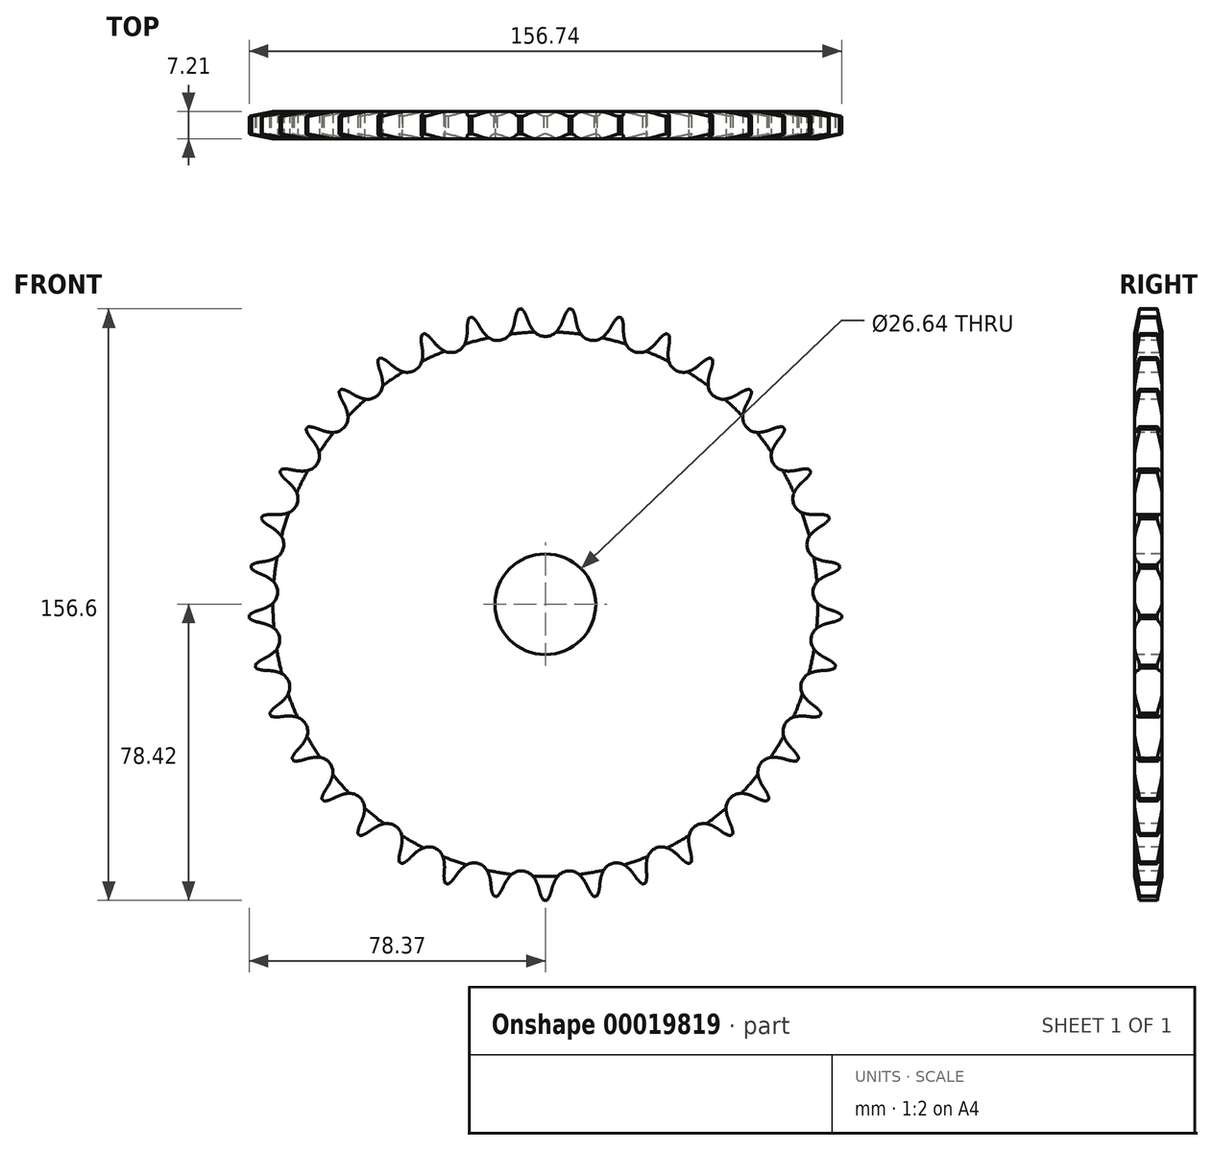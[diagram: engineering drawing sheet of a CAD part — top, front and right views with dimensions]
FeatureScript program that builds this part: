
annotation { "Feature Type Name" : "Feature", "Feature Type Description" : "" }
export const myFeature = defineFeature(function(context is Context, id is Id, definition is map)
    precondition{}
    {
        {
            var Q0;
            Q0=qCreatedBy(makeId("Right.planeOp"),FACE);
            var sketch = newSketch(context, id + "F0", { "sketchPlane" : qUnion([Q0])});
            skLineSegment(sketch, "E0.bottom", {"start": v(0, 78.42) * mm, "end": v(7.21, 78.42) * mm});
            skLineSegment(sketch, "E0.top", {"start": v(0, 13.32) * mm, "end": v(7.21, 13.32) * mm});
            skLineSegment(sketch, "E0.left", {"start": v(0, 78.42) * mm, "end": v(0, 13.32) * mm});
            skLineSegment(sketch, "E0.right", {"start": v(7.21, 78.42) * mm, "end": v(7.21, 13.32) * mm});
            skLineSegment(sketch, "E1", {"start": v(0, 0) * mm, "end": v(19.43, 0) * mm, "construction": true});
            skLineSegment(sketch, "E2.MirrorCS", {"start": v(0, -78.42) * mm, "end": v(7.21, -78.42) * mm});
            skLineSegment(sketch, "E3.MirrorCS", {"start": v(0, -78.42) * mm, "end": v(0, -13.32) * mm});
            skLineSegment(sketch, "E4.MirrorCS", {"start": v(7.21, -78.42) * mm, "end": v(7.21, -13.32) * mm});
            skLineSegment(sketch, "E5.MirrorCS", {"start": v(0, -13.32) * mm, "end": v(7.21, -13.32) * mm});
            skSolve(sketch);
        }
        {
            var Q0;
            Q0=makeQuery(id+"F0.imprint","IMPRINT",FACE,{"disambiguationData":[TD([[makeQuery(id+"F0.imprint","IMPRINT",EDGE,{"derivedFrom":sQuery(id+"F0.wireOp",EDGE,"E0.bottom")}),-1.0]])]});
            var Q1;
            Q1=sQuery(id+"F0.wireOp",EDGE,"E1");
            revolve(context, id + "F1", {"entities" : qUnion([Q0]), "axis" : qUnion([Q1]), "revolveType" : RevolveType.FULL});
        }
        {
            var Q0;
            Q0=makeQuery(id+"F1.opRevolve","SWEPT_EDGE",EDGE,{"disambiguationData":[OSD([sQuery(id+"F0.wireOp",EDGE,"E0.bottom"),sQuery(id+"F0.wireOp",EDGE,"E0.left")])]});
            var Q1;
            Q1=makeQuery(id+"F1.opRevolve","SWEPT_EDGE",EDGE,{"disambiguationData":[OSD([sQuery(id+"F0.wireOp",EDGE,"E0.bottom"),sQuery(id+"F0.wireOp",EDGE,"E0.right")])]});
            chamfer(context, id + "F2", {"entities" : qUnion([Q0, Q1]), "chamferType" : ChamferType.TWO_OFFSETS, "width1" : 1.27 * mm, "oppositeDirection" : true, "width2" : 6.35 * mm, "tangentPropagation" : true});
        }
        {
            var Q0;
            Q0=makeQuery(id+"F1.opRevolve","SWEPT_FACE",FACE,{"disambiguationData":[OSD([sQuery(id+"F0.wireOp",EDGE,"E0.left")])]});
            var sketch = newSketch(context, id + "F3", { "sketchPlane" : qUnion([Q0])});
            skCircle(sketch, "E6", {"center": v(0, 0) * mm, "radius": 74.88 * mm, "construction": true});
            skLineSegment(sketch, "E7", {"start": v(0, 0) * mm, "end": v(0, 74.88) * mm, "construction": true});
            skLineSegment(sketch, "E8", {"start": v(0, 74.88) * mm, "end": v(50.33, 74.88) * mm, "construction": true});
            skLineSegment(sketch, "E9", {"start": v(0, 74.88) * mm, "end": v(5.11, 78.68) * mm, "construction": true});
            skLineSegment(sketch, "E10", {"start": v(5.11, 78.68) * mm, "end": v(-4.63, 75.1) * mm, "construction": true});
            skLineSegment(sketch, "E11", {"start": v(-4.63, 75.1) * mm, "end": v(-4.63, 75.1) * mm});
            skLineSegment(sketch, "E12", {"start": v(0, 0) * mm, "end": v(-6.7, 78.67) * mm, "construction": true});
            skArc(sketch, "E13", {"start": v(-6.7, 78.67) * mm, "mid": v(-16.4, 70.36) * mm, "end": v(-5.01, 76.15) * mm, "construction": true});
            skArc(sketch, "E14", {"start": v(-5.01, 76.15) * mm, "mid": v(-5.7, 77.5) * mm, "end": v(-6.7, 78.67) * mm});
            skLineSegment(sketch, "E15", {"start": v(-5.01, 76.15) * mm, "end": v(-8.52, 85.73) * mm, "construction": true});
            skLineSegment(sketch, "E16", {"start": v(-4.63, 75.1) * mm, "end": v(-5.01, 76.15) * mm});
            skArc(sketch, "E17", {"start": v(-4.63, 75.1) * mm, "mid": v(-4.02, 73.75) * mm, "end": v(-3.22, 72.49) * mm});
            skArc(sketch, "E18", {"start": v(-3.22, 72.49) * mm, "mid": v(14.24, 83.6) * mm, "end": v(-4.63, 75.1) * mm, "construction": true});
            skArc(sketch, "E19", {"start": v(0, 70.87) * mm, "mid": v(1.8, 78.46) * mm, "end": v(-3.22, 72.49) * mm, "construction": true});
            skArc(sketch, "E20", {"start": v(-3.22, 72.49) * mm, "mid": v(-1.8, 71.3) * mm, "end": v(0, 70.87) * mm});
            skArc(sketch, "E21.MirrorCS", {"start": v(3.22, 72.49) * mm, "mid": v(1.8, 71.3) * mm, "end": v(0, 70.87) * mm});
            skArc(sketch, "E22.MirrorCS", {"start": v(4.63, 75.1) * mm, "mid": v(4.02, 73.75) * mm, "end": v(3.22, 72.49) * mm});
            skLineSegment(sketch, "E23.MirrorCS", {"start": v(4.63, 75.1) * mm, "end": v(5.01, 76.15) * mm});
            skArc(sketch, "E24.MirrorCS", {"start": v(5.01, 76.15) * mm, "mid": v(5.7, 77.5) * mm, "end": v(6.7, 78.67) * mm});
            skArc(sketch, "E25.1.0", {"start": v(-17.81, 74.2) * mm, "mid": v(-18.72, 75.43) * mm, "end": v(-19.9, 76.4) * mm});
            skLineSegment(sketch, "E25.1.1", {"start": v(-17.26, 73.24) * mm, "end": v(-17.81, 74.2) * mm});
            skArc(sketch, "E25.1.2", {"start": v(-17.26, 73.24) * mm, "mid": v(-16.42, 72) * mm, "end": v(-15.42, 70.9) * mm});
            skArc(sketch, "E25.1.3", {"start": v(-15.42, 70.9) * mm, "mid": v(-13.82, 69.97) * mm, "end": v(-11.98, 69.85) * mm});
            skArc(sketch, "E25.1.4", {"start": v(-9.08, 71.99) * mm, "mid": v(-10.27, 70.58) * mm, "end": v(-11.98, 69.85) * mm});
            skArc(sketch, "E25.1.5", {"start": v(-8.13, 74.81) * mm, "mid": v(-8.5, 73.37) * mm, "end": v(-9.08, 71.99) * mm});
            skLineSegment(sketch, "E25.1.6", {"start": v(-8.13, 74.81) * mm, "end": v(-7.93, 75.9) * mm});
            skArc(sketch, "E25.1.7", {"start": v(-7.93, 75.9) * mm, "mid": v(-7.48, 77.36) * mm, "end": v(-6.7, 78.67) * mm});
            skArc(sketch, "E25.2.0", {"start": v(-30.1, 70.13) * mm, "mid": v(-31.2, 71.18) * mm, "end": v(-32.52, 71.94) * mm});
            skLineSegment(sketch, "E25.2.1", {"start": v(-29.39, 69.27) * mm, "end": v(-30.1, 70.13) * mm});
            skArc(sketch, "E25.2.2", {"start": v(-29.39, 69.27) * mm, "mid": v(-28.36, 68.2) * mm, "end": v(-27.18, 67.28) * mm});
            skArc(sketch, "E25.2.3", {"start": v(-27.18, 67.28) * mm, "mid": v(-25.45, 66.62) * mm, "end": v(-23.6, 66.82) * mm});
            skArc(sketch, "E25.2.4", {"start": v(-21.11, 69.42) * mm, "mid": v(-22.05, 67.82) * mm, "end": v(-23.6, 66.82) * mm});
            skArc(sketch, "E25.2.5", {"start": v(-20.65, 72.36) * mm, "mid": v(-20.78, 70.87) * mm, "end": v(-21.11, 69.42) * mm});
            skLineSegment(sketch, "E25.2.6", {"start": v(-20.65, 72.36) * mm, "end": v(-20.64, 73.47) * mm});
            skArc(sketch, "E25.2.7", {"start": v(-20.64, 73.47) * mm, "mid": v(-20.44, 74.98) * mm, "end": v(-19.9, 76.4) * mm});
            skArc(sketch, "E25.3.0", {"start": v(-41.52, 64.03) * mm, "mid": v(-42.78, 64.88) * mm, "end": v(-44.21, 65.41) * mm});
            skLineSegment(sketch, "E25.3.1", {"start": v(-40.67, 63.31) * mm, "end": v(-41.52, 64.03) * mm});
            skArc(sketch, "E25.3.2", {"start": v(-40.67, 63.31) * mm, "mid": v(-39.48, 62.42) * mm, "end": v(-38.16, 61.71) * mm});
            skArc(sketch, "E25.3.3", {"start": v(-38.16, 61.71) * mm, "mid": v(-36.34, 61.37) * mm, "end": v(-34.56, 61.87) * mm});
            skArc(sketch, "E25.3.4", {"start": v(-32.54, 64.85) * mm, "mid": v(-33.2, 63.12) * mm, "end": v(-34.56, 61.87) * mm});
            skArc(sketch, "E25.3.5", {"start": v(-32.59, 67.83) * mm, "mid": v(-32.46, 66.34) * mm, "end": v(-32.54, 64.85) * mm});
            skLineSegment(sketch, "E25.3.6", {"start": v(-32.59, 67.83) * mm, "end": v(-32.76, 68.92) * mm});
            skArc(sketch, "E25.3.7", {"start": v(-32.76, 68.92) * mm, "mid": v(-32.82, 70.45) * mm, "end": v(-32.52, 71.94) * mm});
            skArc(sketch, "E25.4.0", {"start": v(-51.74, 56.1) * mm, "mid": v(-53.13, 56.72) * mm, "end": v(-54.63, 57) * mm});
            skLineSegment(sketch, "E25.4.1", {"start": v(-50.79, 55.53) * mm, "end": v(-51.74, 56.1) * mm});
            skArc(sketch, "E25.4.2", {"start": v(-50.79, 55.53) * mm, "mid": v(-49.46, 54.85) * mm, "end": v(-48.04, 54.38) * mm});
            skArc(sketch, "E25.4.3", {"start": v(-48.04, 54.38) * mm, "mid": v(-46.2, 54.34) * mm, "end": v(-44.52, 55.14) * mm});
            skArc(sketch, "E25.4.4", {"start": v(-43.03, 58.42) * mm, "mid": v(-43.39, 56.6) * mm, "end": v(-44.52, 55.14) * mm});
            skArc(sketch, "E25.4.5", {"start": v(-43.58, 61.35) * mm, "mid": v(-43.2, 59.9) * mm, "end": v(-43.03, 58.42) * mm});
            skLineSegment(sketch, "E25.4.6", {"start": v(-43.58, 61.35) * mm, "end": v(-43.94, 62.4) * mm});
            skArc(sketch, "E25.4.7", {"start": v(-43.94, 62.4) * mm, "mid": v(-44.25, 63.89) * mm, "end": v(-44.21, 65.41) * mm});
            skArc(sketch, "E25.5.0", {"start": v(-60.48, 46.55) * mm, "mid": v(-61.95, 46.93) * mm, "end": v(-63.48, 46.95) * mm});
            skLineSegment(sketch, "E25.5.1", {"start": v(-59.44, 46.14) * mm, "end": v(-60.48, 46.55) * mm});
            skArc(sketch, "E25.5.2", {"start": v(-59.44, 46.14) * mm, "mid": v(-58.02, 45.7) * mm, "end": v(-56.54, 45.48) * mm});
            skArc(sketch, "E25.5.3", {"start": v(-56.54, 45.48) * mm, "mid": v(-54.71, 45.75) * mm, "end": v(-53.2, 46.82) * mm});
            skArc(sketch, "E25.5.4", {"start": v(-52.29, 50.3) * mm, "mid": v(-52.33, 48.46) * mm, "end": v(-53.2, 46.82) * mm});
            skArc(sketch, "E25.5.5", {"start": v(-53.32, 53.1) * mm, "mid": v(-52.7, 51.74) * mm, "end": v(-52.29, 50.3) * mm});
            skLineSegment(sketch, "E25.5.6", {"start": v(-53.32, 53.1) * mm, "end": v(-53.85, 54.07) * mm});
            skArc(sketch, "E25.5.7", {"start": v(-53.85, 54.07) * mm, "mid": v(-54.42, 55.5) * mm, "end": v(-54.63, 57) * mm});
            skArc(sketch, "E25.6.0", {"start": v(-67.47, 35.66) * mm, "mid": v(-69, 35.78) * mm, "end": v(-70.5, 35.54) * mm});
            skLineSegment(sketch, "E25.6.1", {"start": v(-66.39, 35.43) * mm, "end": v(-67.47, 35.66) * mm});
            skArc(sketch, "E25.6.2", {"start": v(-66.39, 35.43) * mm, "mid": v(-64.9, 35.24) * mm, "end": v(-63.41, 35.27) * mm});
            skArc(sketch, "E25.6.3", {"start": v(-63.41, 35.27) * mm, "mid": v(-61.66, 35.85) * mm, "end": v(-60.35, 37.16) * mm});
            skArc(sketch, "E25.6.4", {"start": v(-60.04, 40.75) * mm, "mid": v(-59.77, 38.92) * mm, "end": v(-60.35, 37.16) * mm});
            skArc(sketch, "E25.6.5", {"start": v(-61.53, 43.32) * mm, "mid": v(-60.7, 42.09) * mm, "end": v(-60.04, 40.75) * mm});
            skLineSegment(sketch, "E25.6.6", {"start": v(-61.53, 43.32) * mm, "end": v(-62.21, 44.2) * mm});
            skArc(sketch, "E25.6.7", {"start": v(-62.21, 44.2) * mm, "mid": v(-63.01, 45.5) * mm, "end": v(-63.48, 46.95) * mm});
            skArc(sketch, "E25.7.0", {"start": v(-72.53, 23.74) * mm, "mid": v(-74.05, 23.6) * mm, "end": v(-75.5, 23.12) * mm});
            skLineSegment(sketch, "E25.7.1", {"start": v(-71.42, 23.7) * mm, "end": v(-72.53, 23.74) * mm});
            skArc(sketch, "E25.7.2", {"start": v(-71.42, 23.7) * mm, "mid": v(-69.93, 23.77) * mm, "end": v(-68.46, 24.04) * mm});
            skArc(sketch, "E25.7.3", {"start": v(-68.46, 24.04) * mm, "mid": v(-66.83, 24.91) * mm, "end": v(-65.76, 26.42) * mm});
            skArc(sketch, "E25.7.4", {"start": v(-66.06, 30.01) * mm, "mid": v(-65.48, 28.25) * mm, "end": v(-65.76, 26.42) * mm});
            skArc(sketch, "E25.7.5", {"start": v(-67.96, 32.3) * mm, "mid": v(-66.93, 31.23) * mm, "end": v(-66.06, 30.01) * mm});
            skLineSegment(sketch, "E25.7.6", {"start": v(-67.96, 32.3) * mm, "end": v(-68.79, 33.05) * mm});
            skArc(sketch, "E25.7.7", {"start": v(-68.79, 33.05) * mm, "mid": v(-69.8, 34.2) * mm, "end": v(-70.5, 35.54) * mm});
            skArc(sketch, "E25.8.0", {"start": v(-75.5, 11.14) * mm, "mid": v(-76.97, 10.75) * mm, "end": v(-78.31, 10.03) * mm});
            skLineSegment(sketch, "E25.8.1", {"start": v(-74.4, 11.3) * mm, "end": v(-75.5, 11.14) * mm});
            skArc(sketch, "E25.8.2", {"start": v(-74.4, 11.3) * mm, "mid": v(-72.94, 11.6) * mm, "end": v(-71.54, 12.13) * mm});
            skArc(sketch, "E25.8.3", {"start": v(-71.54, 12.13) * mm, "mid": v(-70.08, 13.26) * mm, "end": v(-69.28, 14.93) * mm});
            skArc(sketch, "E25.8.4", {"start": v(-70.18, 18.42) * mm, "mid": v(-69.32, 16.78) * mm, "end": v(-69.28, 14.93) * mm});
            skArc(sketch, "E25.8.5", {"start": v(-72.45, 20.35) * mm, "mid": v(-71.24, 19.47) * mm, "end": v(-70.18, 18.42) * mm});
            skLineSegment(sketch, "E25.8.6", {"start": v(-72.45, 20.35) * mm, "end": v(-73.38, 20.94) * mm});
            skArc(sketch, "E25.8.7", {"start": v(-73.38, 20.94) * mm, "mid": v(-74.57, 21.9) * mm, "end": v(-75.5, 23.12) * mm});
            skArc(sketch, "E25.9.0", {"start": v(-76.3, -1.78) * mm, "mid": v(-77.68, -2.4) * mm, "end": v(-78.88, -3.35) * mm});
            skLineSegment(sketch, "E25.9.1", {"start": v(-75.24, -1.44) * mm, "end": v(-76.3, -1.78) * mm});
            skArc(sketch, "E25.9.2", {"start": v(-75.24, -1.44) * mm, "mid": v(-73.85, -0.89) * mm, "end": v(-72.56, -0.14) * mm});
            skArc(sketch, "E25.9.3", {"start": v(-72.56, -0.14) * mm, "mid": v(-71.3, 1.23) * mm, "end": v(-70.8, 3) * mm});
            skArc(sketch, "E25.9.4", {"start": v(-72.29, 6.3) * mm, "mid": v(-71.16, 4.82) * mm, "end": v(-70.8, 3) * mm});
            skArc(sketch, "E25.9.5", {"start": v(-74.84, 7.82) * mm, "mid": v(-73.5, 7.15) * mm, "end": v(-72.29, 6.3) * mm});
            skLineSegment(sketch, "E25.9.6", {"start": v(-74.84, 7.82) * mm, "end": v(-75.87, 8.24) * mm});
            skArc(sketch, "E25.9.7", {"start": v(-75.87, 8.24) * mm, "mid": v(-77.2, 8.99) * mm, "end": v(-78.31, 10.03) * mm});
            skArc(sketch, "E25.10.0", {"start": v(-74.9, -14.65) * mm, "mid": v(-76.16, -15.5) * mm, "end": v(-77.18, -16.63) * mm});
            skLineSegment(sketch, "E25.10.1", {"start": v(-73.91, -14.14) * mm, "end": v(-74.9, -14.65) * mm});
            skArc(sketch, "E25.10.2", {"start": v(-73.91, -14.14) * mm, "mid": v(-72.64, -13.35) * mm, "end": v(-71.5, -12.4) * mm});
            skArc(sketch, "E25.10.3", {"start": v(-71.5, -12.4) * mm, "mid": v(-70.5, -10.84) * mm, "end": v(-70.3, -9) * mm});
            skArc(sketch, "E25.10.4", {"start": v(-72.3, -6.02) * mm, "mid": v(-70.95, -7.27) * mm, "end": v(-70.3, -9) * mm});
            skArc(sketch, "E25.10.5", {"start": v(-75.09, -4.95) * mm, "mid": v(-73.66, -5.38) * mm, "end": v(-72.3, -6.02) * mm});
            skLineSegment(sketch, "E25.10.6", {"start": v(-75.09, -4.95) * mm, "end": v(-76.17, -4.7) * mm});
            skArc(sketch, "E25.10.7", {"start": v(-76.17, -4.7) * mm, "mid": v(-77.6, -4.19) * mm, "end": v(-78.88, -3.35) * mm});
            skArc(sketch, "E25.11.0", {"start": v(-71.34, -27.1) * mm, "mid": v(-72.44, -28.15) * mm, "end": v(-73.26, -29.44) * mm});
            skLineSegment(sketch, "E25.11.1", {"start": v(-70.46, -26.42) * mm, "end": v(-71.34, -27.1) * mm});
            skArc(sketch, "E25.11.2", {"start": v(-70.46, -26.42) * mm, "mid": v(-69.34, -25.44) * mm, "end": v(-68.37, -24.3) * mm});
            skArc(sketch, "E25.11.3", {"start": v(-68.37, -24.3) * mm, "mid": v(-67.64, -22.6) * mm, "end": v(-67.76, -20.75) * mm});
            skArc(sketch, "E25.11.4", {"start": v(-70.25, -18.15) * mm, "mid": v(-68.7, -19.16) * mm, "end": v(-67.76, -20.75) * mm});
            skArc(sketch, "E25.11.5", {"start": v(-73.17, -17.56) * mm, "mid": v(-71.7, -17.75) * mm, "end": v(-70.25, -18.15) * mm});
            skLineSegment(sketch, "E25.11.6", {"start": v(-73.17, -17.56) * mm, "end": v(-74.28, -17.5) * mm});
            skArc(sketch, "E25.11.7", {"start": v(-74.28, -17.5) * mm, "mid": v(-75.78, -17.24) * mm, "end": v(-77.18, -16.63) * mm});
            skArc(sketch, "E25.12.0", {"start": v(-65.74, -38.76) * mm, "mid": v(-66.64, -39.99) * mm, "end": v(-67.23, -41.4) * mm});
            skLineSegment(sketch, "E25.12.1", {"start": v(-64.98, -37.95) * mm, "end": v(-65.74, -38.76) * mm});
            skArc(sketch, "E25.12.2", {"start": v(-64.98, -37.95) * mm, "mid": v(-64.04, -36.8) * mm, "end": v(-63.28, -35.5) * mm});
            skArc(sketch, "E25.12.3", {"start": v(-63.28, -35.5) * mm, "mid": v(-62.85, -33.7) * mm, "end": v(-63.28, -31.9) * mm});
            skArc(sketch, "E25.12.4", {"start": v(-66.17, -29.76) * mm, "mid": v(-64.47, -30.5) * mm, "end": v(-63.28, -31.9) * mm});
            skArc(sketch, "E25.12.5", {"start": v(-69.15, -29.68) * mm, "mid": v(-67.66, -29.61) * mm, "end": v(-66.17, -29.76) * mm});
            skLineSegment(sketch, "E25.12.6", {"start": v(-69.15, -29.68) * mm, "end": v(-70.25, -29.8) * mm});
            skArc(sketch, "E25.12.7", {"start": v(-70.25, -29.8) * mm, "mid": v(-71.78, -29.8) * mm, "end": v(-73.26, -29.44) * mm});
            skArc(sketch, "E25.13.0", {"start": v(-58.24, -49.31) * mm, "mid": v(-58.92, -50.68) * mm, "end": v(-59.27, -52.16) * mm});
            skLineSegment(sketch, "E25.13.1", {"start": v(-57.63, -48.39) * mm, "end": v(-58.24, -49.31) * mm});
            skArc(sketch, "E25.13.2", {"start": v(-57.63, -48.39) * mm, "mid": v(-56.9, -47.08) * mm, "end": v(-56.37, -45.7) * mm});
            skArc(sketch, "E25.13.3", {"start": v(-56.37, -45.7) * mm, "mid": v(-56.25, -43.84) * mm, "end": v(-56.98, -42.14) * mm});
            skArc(sketch, "E25.13.4", {"start": v(-60.2, -40.52) * mm, "mid": v(-58.4, -40.95) * mm, "end": v(-56.98, -42.14) * mm});
            skArc(sketch, "E25.13.5", {"start": v(-63.14, -40.94) * mm, "mid": v(-61.68, -40.62) * mm, "end": v(-60.2, -40.52) * mm});
            skLineSegment(sketch, "E25.13.6", {"start": v(-63.14, -40.94) * mm, "end": v(-64.2, -41.25) * mm});
            skArc(sketch, "E25.13.7", {"start": v(-64.2, -41.25) * mm, "mid": v(-65.7, -41.5) * mm, "end": v(-67.23, -41.4) * mm});
            skArc(sketch, "E25.14.0", {"start": v(-49.07, -58.45) * mm, "mid": v(-49.51, -59.9) * mm, "end": v(-49.6, -61.43) * mm});
            skLineSegment(sketch, "E25.14.1", {"start": v(-48.63, -57.43) * mm, "end": v(-49.07, -58.45) * mm});
            skArc(sketch, "E25.14.2", {"start": v(-48.63, -57.43) * mm, "mid": v(-48.13, -56.02) * mm, "end": v(-47.83, -54.56) * mm});
            skArc(sketch, "E25.14.3", {"start": v(-47.83, -54.56) * mm, "mid": v(-48.03, -52.72) * mm, "end": v(-49.04, -51.17) * mm});
            skArc(sketch, "E25.14.4", {"start": v(-52.48, -50.1) * mm, "mid": v(-50.63, -50.23) * mm, "end": v(-49.04, -51.17) * mm});
            skArc(sketch, "E25.14.5", {"start": v(-55.31, -51.02) * mm, "mid": v(-53.93, -50.46) * mm, "end": v(-52.48, -50.1) * mm});
            skLineSegment(sketch, "E25.14.6", {"start": v(-55.31, -51.02) * mm, "end": v(-56.31, -51.5) * mm});
            skArc(sketch, "E25.14.7", {"start": v(-56.31, -51.5) * mm, "mid": v(-57.75, -52.01) * mm, "end": v(-59.27, -52.16) * mm});
            skArc(sketch, "E25.15.0", {"start": v(-38.49, -65.9) * mm, "mid": v(-38.68, -67.41) * mm, "end": v(-38.5, -68.93) * mm});
            skLineSegment(sketch, "E25.15.1", {"start": v(-38.22, -64.82) * mm, "end": v(-38.49, -65.9) * mm});
            skArc(sketch, "E25.15.2", {"start": v(-38.22, -64.82) * mm, "mid": v(-37.97, -63.35) * mm, "end": v(-37.93, -61.86) * mm});
            skArc(sketch, "E25.15.3", {"start": v(-37.93, -61.86) * mm, "mid": v(-38.43, -60.08) * mm, "end": v(-39.69, -58.72) * mm});
            skArc(sketch, "E25.15.4", {"start": v(-43.26, -58.26) * mm, "mid": v(-41.42, -58.06) * mm, "end": v(-39.69, -58.72) * mm});
            skArc(sketch, "E25.15.5", {"start": v(-45.9, -59.63) * mm, "mid": v(-44.63, -58.85) * mm, "end": v(-43.26, -58.26) * mm});
            skLineSegment(sketch, "E25.15.6", {"start": v(-45.9, -59.63) * mm, "end": v(-46.8, -60.28) * mm});
            skArc(sketch, "E25.15.7", {"start": v(-46.8, -60.28) * mm, "mid": v(-48.13, -61.02) * mm, "end": v(-49.6, -61.43) * mm});
            skArc(sketch, "E25.16.0", {"start": v(-26.8, -71.45) * mm, "mid": v(-26.73, -72.98) * mm, "end": v(-26.3, -74.44) * mm});
            skLineSegment(sketch, "E25.16.1", {"start": v(-26.72, -70.35) * mm, "end": v(-26.8, -71.45) * mm});
            skArc(sketch, "E25.16.2", {"start": v(-26.72, -70.35) * mm, "mid": v(-26.71, -68.86) * mm, "end": v(-26.93, -67.38) * mm});
            skArc(sketch, "E25.16.3", {"start": v(-26.93, -67.38) * mm, "mid": v(-27.73, -65.7) * mm, "end": v(-29.2, -64.58) * mm});
            skArc(sketch, "E25.16.4", {"start": v(-32.79, -64.73) * mm, "mid": v(-31, -64.23) * mm, "end": v(-29.2, -64.58) * mm});
            skArc(sketch, "E25.16.5", {"start": v(-35.16, -66.53) * mm, "mid": v(-34.04, -65.54) * mm, "end": v(-32.79, -64.73) * mm});
            skLineSegment(sketch, "E25.16.6", {"start": v(-35.16, -66.53) * mm, "end": v(-35.94, -67.32) * mm});
            skArc(sketch, "E25.16.7", {"start": v(-35.94, -67.32) * mm, "mid": v(-37.12, -68.28) * mm, "end": v(-38.5, -68.93) * mm});
            skArc(sketch, "E25.17.0", {"start": v(-14.34, -74.96) * mm, "mid": v(-14.01, -76.45) * mm, "end": v(-13.34, -77.82) * mm});
            skLineSegment(sketch, "E25.17.1", {"start": v(-14.44, -73.85) * mm, "end": v(-14.34, -74.96) * mm});
            skArc(sketch, "E25.17.2", {"start": v(-14.44, -73.85) * mm, "mid": v(-14.7, -72.38) * mm, "end": v(-15.15, -70.96) * mm});
            skArc(sketch, "E25.17.3", {"start": v(-15.15, -70.96) * mm, "mid": v(-16.22, -69.45) * mm, "end": v(-17.86, -68.58) * mm});
            skArc(sketch, "E25.17.4", {"start": v(-21.38, -69.34) * mm, "mid": v(-19.7, -68.54) * mm, "end": v(-17.86, -68.58) * mm});
            skArc(sketch, "E25.17.5", {"start": v(-23.4, -71.52) * mm, "mid": v(-22.47, -70.35) * mm, "end": v(-21.38, -69.34) * mm});
            skLineSegment(sketch, "E25.17.6", {"start": v(-23.4, -71.52) * mm, "end": v(-24.04, -72.43) * mm});
            skArc(sketch, "E25.17.7", {"start": v(-24.04, -72.43) * mm, "mid": v(-25.05, -73.57) * mm, "end": v(-26.3, -74.44) * mm});
            skArc(sketch, "E25.18.0", {"start": v(-1.46, -76.3) * mm, "mid": v(-0.89, -77.71) * mm, "end": v(0, -78.95) * mm});
            skLineSegment(sketch, "E25.18.1", {"start": v(-1.75, -75.23) * mm, "end": v(-1.46, -76.3) * mm});
            skArc(sketch, "E25.18.2", {"start": v(-1.75, -75.23) * mm, "mid": v(-2.25, -73.82) * mm, "end": v(-2.94, -72.5) * mm});
            skArc(sketch, "E25.18.3", {"start": v(-2.94, -72.5) * mm, "mid": v(-4.25, -71.2) * mm, "end": v(-6.01, -70.62) * mm});
            skArc(sketch, "E25.18.4", {"start": v(-9.35, -71.95) * mm, "mid": v(-7.84, -70.89) * mm, "end": v(-6.01, -70.62) * mm});
            skArc(sketch, "E25.18.5", {"start": v(-10.99, -74.44) * mm, "mid": v(-10.26, -73.14) * mm, "end": v(-9.35, -71.95) * mm});
            skLineSegment(sketch, "E25.18.6", {"start": v(-10.99, -74.44) * mm, "end": v(-11.45, -75.45) * mm});
            skArc(sketch, "E25.18.7", {"start": v(-11.45, -75.45) * mm, "mid": v(-12.26, -76.75) * mm, "end": v(-13.34, -77.82) * mm});
            skArc(sketch, "E25.19.0", {"start": v(11.45, -75.45) * mm, "mid": v(12.26, -76.75) * mm, "end": v(13.34, -77.82) * mm});
            skLineSegment(sketch, "E25.19.1", {"start": v(10.99, -74.44) * mm, "end": v(11.45, -75.45) * mm});
            skArc(sketch, "E25.19.2", {"start": v(10.99, -74.44) * mm, "mid": v(10.26, -73.14) * mm, "end": v(9.35, -71.95) * mm});
            skArc(sketch, "E25.19.3", {"start": v(9.35, -71.95) * mm, "mid": v(7.84, -70.89) * mm, "end": v(6.01, -70.62) * mm});
            skArc(sketch, "E25.19.4", {"start": v(2.94, -72.5) * mm, "mid": v(4.25, -71.2) * mm, "end": v(6.01, -70.62) * mm});
            skArc(sketch, "E25.19.5", {"start": v(1.75, -75.23) * mm, "mid": v(2.25, -73.82) * mm, "end": v(2.94, -72.5) * mm});
            skLineSegment(sketch, "E25.19.6", {"start": v(1.75, -75.23) * mm, "end": v(1.46, -76.3) * mm});
            skArc(sketch, "E25.19.7", {"start": v(1.46, -76.3) * mm, "mid": v(0.89, -77.71) * mm, "end": v(0, -78.95) * mm});
            skArc(sketch, "E25.20.0", {"start": v(24.04, -72.43) * mm, "mid": v(25.05, -73.57) * mm, "end": v(26.3, -74.44) * mm});
            skLineSegment(sketch, "E25.20.1", {"start": v(23.4, -71.52) * mm, "end": v(24.04, -72.43) * mm});
            skArc(sketch, "E25.20.2", {"start": v(23.4, -71.52) * mm, "mid": v(22.47, -70.35) * mm, "end": v(21.38, -69.34) * mm});
            skArc(sketch, "E25.20.3", {"start": v(21.38, -69.34) * mm, "mid": v(19.7, -68.54) * mm, "end": v(17.86, -68.58) * mm});
            skArc(sketch, "E25.20.4", {"start": v(15.15, -70.96) * mm, "mid": v(16.22, -69.45) * mm, "end": v(17.86, -68.58) * mm});
            skArc(sketch, "E25.20.5", {"start": v(14.44, -73.85) * mm, "mid": v(14.7, -72.38) * mm, "end": v(15.15, -70.96) * mm});
            skLineSegment(sketch, "E25.20.6", {"start": v(14.44, -73.85) * mm, "end": v(14.34, -74.96) * mm});
            skArc(sketch, "E25.20.7", {"start": v(14.34, -74.96) * mm, "mid": v(14.01, -76.45) * mm, "end": v(13.34, -77.82) * mm});
            skArc(sketch, "E25.21.0", {"start": v(35.94, -67.32) * mm, "mid": v(37.12, -68.28) * mm, "end": v(38.5, -68.93) * mm});
            skLineSegment(sketch, "E25.21.1", {"start": v(35.16, -66.53) * mm, "end": v(35.94, -67.32) * mm});
            skArc(sketch, "E25.21.2", {"start": v(35.16, -66.53) * mm, "mid": v(34.04, -65.54) * mm, "end": v(32.79, -64.73) * mm});
            skArc(sketch, "E25.21.3", {"start": v(32.79, -64.73) * mm, "mid": v(31, -64.23) * mm, "end": v(29.2, -64.58) * mm});
            skArc(sketch, "E25.21.4", {"start": v(26.93, -67.38) * mm, "mid": v(27.73, -65.7) * mm, "end": v(29.2, -64.58) * mm});
            skArc(sketch, "E25.21.5", {"start": v(26.72, -70.35) * mm, "mid": v(26.71, -68.86) * mm, "end": v(26.93, -67.38) * mm});
            skLineSegment(sketch, "E25.21.6", {"start": v(26.72, -70.35) * mm, "end": v(26.8, -71.45) * mm});
            skArc(sketch, "E25.21.7", {"start": v(26.8, -71.45) * mm, "mid": v(26.73, -72.98) * mm, "end": v(26.3, -74.44) * mm});
            skArc(sketch, "E25.22.0", {"start": v(46.8, -60.28) * mm, "mid": v(48.13, -61.02) * mm, "end": v(49.6, -61.43) * mm});
            skLineSegment(sketch, "E25.22.1", {"start": v(45.9, -59.63) * mm, "end": v(46.8, -60.28) * mm});
            skArc(sketch, "E25.22.2", {"start": v(45.9, -59.63) * mm, "mid": v(44.63, -58.85) * mm, "end": v(43.26, -58.26) * mm});
            skArc(sketch, "E25.22.3", {"start": v(43.26, -58.26) * mm, "mid": v(41.42, -58.06) * mm, "end": v(39.69, -58.72) * mm});
            skArc(sketch, "E25.22.4", {"start": v(37.93, -61.86) * mm, "mid": v(38.43, -60.08) * mm, "end": v(39.69, -58.72) * mm});
            skArc(sketch, "E25.22.5", {"start": v(38.22, -64.82) * mm, "mid": v(37.97, -63.35) * mm, "end": v(37.93, -61.86) * mm});
            skLineSegment(sketch, "E25.22.6", {"start": v(38.22, -64.82) * mm, "end": v(38.49, -65.9) * mm});
            skArc(sketch, "E25.22.7", {"start": v(38.49, -65.9) * mm, "mid": v(38.68, -67.41) * mm, "end": v(38.5, -68.93) * mm});
            skArc(sketch, "E25.23.0", {"start": v(56.31, -51.5) * mm, "mid": v(57.75, -52.01) * mm, "end": v(59.27, -52.16) * mm});
            skLineSegment(sketch, "E25.23.1", {"start": v(55.31, -51.02) * mm, "end": v(56.31, -51.5) * mm});
            skArc(sketch, "E25.23.2", {"start": v(55.31, -51.02) * mm, "mid": v(53.93, -50.46) * mm, "end": v(52.48, -50.1) * mm});
            skArc(sketch, "E25.23.3", {"start": v(52.48, -50.1) * mm, "mid": v(50.63, -50.23) * mm, "end": v(49.04, -51.17) * mm});
            skArc(sketch, "E25.23.4", {"start": v(47.83, -54.56) * mm, "mid": v(48.03, -52.72) * mm, "end": v(49.04, -51.17) * mm});
            skArc(sketch, "E25.23.5", {"start": v(48.63, -57.43) * mm, "mid": v(48.13, -56.02) * mm, "end": v(47.83, -54.56) * mm});
            skLineSegment(sketch, "E25.23.6", {"start": v(48.63, -57.43) * mm, "end": v(49.07, -58.45) * mm});
            skArc(sketch, "E25.23.7", {"start": v(49.07, -58.45) * mm, "mid": v(49.51, -59.9) * mm, "end": v(49.6, -61.43) * mm});
            skArc(sketch, "E25.24.0", {"start": v(64.2, -41.25) * mm, "mid": v(65.7, -41.5) * mm, "end": v(67.23, -41.4) * mm});
            skLineSegment(sketch, "E25.24.1", {"start": v(63.14, -40.94) * mm, "end": v(64.2, -41.25) * mm});
            skArc(sketch, "E25.24.2", {"start": v(63.14, -40.94) * mm, "mid": v(61.68, -40.62) * mm, "end": v(60.2, -40.52) * mm});
            skArc(sketch, "E25.24.3", {"start": v(60.2, -40.52) * mm, "mid": v(58.4, -40.95) * mm, "end": v(56.98, -42.14) * mm});
            skArc(sketch, "E25.24.4", {"start": v(56.37, -45.7) * mm, "mid": v(56.25, -43.84) * mm, "end": v(56.98, -42.14) * mm});
            skArc(sketch, "E25.24.5", {"start": v(57.63, -48.39) * mm, "mid": v(56.9, -47.08) * mm, "end": v(56.37, -45.7) * mm});
            skLineSegment(sketch, "E25.24.6", {"start": v(57.63, -48.39) * mm, "end": v(58.24, -49.31) * mm});
            skArc(sketch, "E25.24.7", {"start": v(58.24, -49.31) * mm, "mid": v(58.92, -50.68) * mm, "end": v(59.27, -52.16) * mm});
            skArc(sketch, "E25.25.0", {"start": v(70.25, -29.8) * mm, "mid": v(71.78, -29.8) * mm, "end": v(73.26, -29.44) * mm});
            skLineSegment(sketch, "E25.25.1", {"start": v(69.15, -29.68) * mm, "end": v(70.25, -29.8) * mm});
            skArc(sketch, "E25.25.2", {"start": v(69.15, -29.68) * mm, "mid": v(67.66, -29.61) * mm, "end": v(66.17, -29.76) * mm});
            skArc(sketch, "E25.25.3", {"start": v(66.17, -29.76) * mm, "mid": v(64.47, -30.5) * mm, "end": v(63.28, -31.9) * mm});
            skArc(sketch, "E25.25.4", {"start": v(63.28, -35.5) * mm, "mid": v(62.85, -33.7) * mm, "end": v(63.28, -31.9) * mm});
            skArc(sketch, "E25.25.5", {"start": v(64.98, -37.95) * mm, "mid": v(64.04, -36.8) * mm, "end": v(63.28, -35.5) * mm});
            skLineSegment(sketch, "E25.25.6", {"start": v(64.98, -37.95) * mm, "end": v(65.74, -38.76) * mm});
            skArc(sketch, "E25.25.7", {"start": v(65.74, -38.76) * mm, "mid": v(66.64, -39.99) * mm, "end": v(67.23, -41.4) * mm});
            skArc(sketch, "E25.26.0", {"start": v(74.28, -17.5) * mm, "mid": v(75.78, -17.24) * mm, "end": v(77.18, -16.63) * mm});
            skLineSegment(sketch, "E25.26.1", {"start": v(73.17, -17.56) * mm, "end": v(74.28, -17.5) * mm});
            skArc(sketch, "E25.26.2", {"start": v(73.17, -17.56) * mm, "mid": v(71.7, -17.75) * mm, "end": v(70.25, -18.15) * mm});
            skArc(sketch, "E25.26.3", {"start": v(70.25, -18.15) * mm, "mid": v(68.7, -19.16) * mm, "end": v(67.76, -20.75) * mm});
            skArc(sketch, "E25.26.4", {"start": v(68.37, -24.3) * mm, "mid": v(67.64, -22.6) * mm, "end": v(67.76, -20.75) * mm});
            skArc(sketch, "E25.26.5", {"start": v(70.46, -26.42) * mm, "mid": v(69.34, -25.44) * mm, "end": v(68.37, -24.3) * mm});
            skLineSegment(sketch, "E25.26.6", {"start": v(70.46, -26.42) * mm, "end": v(71.34, -27.1) * mm});
            skArc(sketch, "E25.26.7", {"start": v(71.34, -27.1) * mm, "mid": v(72.44, -28.15) * mm, "end": v(73.26, -29.44) * mm});
            skArc(sketch, "E25.27.0", {"start": v(76.17, -4.7) * mm, "mid": v(77.6, -4.19) * mm, "end": v(78.88, -3.35) * mm});
            skLineSegment(sketch, "E25.27.1", {"start": v(75.09, -4.95) * mm, "end": v(76.17, -4.7) * mm});
            skArc(sketch, "E25.27.2", {"start": v(75.09, -4.95) * mm, "mid": v(73.66, -5.38) * mm, "end": v(72.3, -6.02) * mm});
            skArc(sketch, "E25.27.3", {"start": v(72.3, -6.02) * mm, "mid": v(70.95, -7.27) * mm, "end": v(70.3, -9) * mm});
            skArc(sketch, "E25.27.4", {"start": v(71.5, -12.4) * mm, "mid": v(70.5, -10.84) * mm, "end": v(70.3, -9) * mm});
            skArc(sketch, "E25.27.5", {"start": v(73.91, -14.14) * mm, "mid": v(72.64, -13.35) * mm, "end": v(71.5, -12.4) * mm});
            skLineSegment(sketch, "E25.27.6", {"start": v(73.91, -14.14) * mm, "end": v(74.9, -14.65) * mm});
            skArc(sketch, "E25.27.7", {"start": v(74.9, -14.65) * mm, "mid": v(76.16, -15.5) * mm, "end": v(77.18, -16.63) * mm});
            skArc(sketch, "E25.28.0", {"start": v(75.87, 8.24) * mm, "mid": v(77.2, 8.99) * mm, "end": v(78.31, 10.03) * mm});
            skLineSegment(sketch, "E25.28.1", {"start": v(74.84, 7.82) * mm, "end": v(75.87, 8.24) * mm});
            skArc(sketch, "E25.28.2", {"start": v(74.84, 7.82) * mm, "mid": v(73.5, 7.15) * mm, "end": v(72.29, 6.3) * mm});
            skArc(sketch, "E25.28.3", {"start": v(72.29, 6.3) * mm, "mid": v(71.16, 4.82) * mm, "end": v(70.8, 3) * mm});
            skArc(sketch, "E25.28.4", {"start": v(72.56, -0.14) * mm, "mid": v(71.3, 1.23) * mm, "end": v(70.8, 3) * mm});
            skArc(sketch, "E25.28.5", {"start": v(75.24, -1.44) * mm, "mid": v(73.85, -0.89) * mm, "end": v(72.56, -0.14) * mm});
            skLineSegment(sketch, "E25.28.6", {"start": v(75.24, -1.44) * mm, "end": v(76.3, -1.78) * mm});
            skArc(sketch, "E25.28.7", {"start": v(76.3, -1.78) * mm, "mid": v(77.68, -2.4) * mm, "end": v(78.88, -3.35) * mm});
            skArc(sketch, "E25.29.0", {"start": v(73.38, 20.94) * mm, "mid": v(74.57, 21.9) * mm, "end": v(75.5, 23.12) * mm});
            skLineSegment(sketch, "E25.29.1", {"start": v(72.45, 20.35) * mm, "end": v(73.38, 20.94) * mm});
            skArc(sketch, "E25.29.2", {"start": v(72.45, 20.35) * mm, "mid": v(71.24, 19.47) * mm, "end": v(70.18, 18.42) * mm});
            skArc(sketch, "E25.29.3", {"start": v(70.18, 18.42) * mm, "mid": v(69.32, 16.78) * mm, "end": v(69.28, 14.93) * mm});
            skArc(sketch, "E25.29.4", {"start": v(71.54, 12.13) * mm, "mid": v(70.08, 13.26) * mm, "end": v(69.28, 14.93) * mm});
            skArc(sketch, "E25.29.5", {"start": v(74.4, 11.3) * mm, "mid": v(72.94, 11.6) * mm, "end": v(71.54, 12.13) * mm});
            skLineSegment(sketch, "E25.29.6", {"start": v(74.4, 11.3) * mm, "end": v(75.5, 11.14) * mm});
            skArc(sketch, "E25.29.7", {"start": v(75.5, 11.14) * mm, "mid": v(76.97, 10.75) * mm, "end": v(78.31, 10.03) * mm});
            skArc(sketch, "E25.30.0", {"start": v(68.79, 33.05) * mm, "mid": v(69.8, 34.2) * mm, "end": v(70.5, 35.54) * mm});
            skLineSegment(sketch, "E25.30.1", {"start": v(67.96, 32.3) * mm, "end": v(68.79, 33.05) * mm});
            skArc(sketch, "E25.30.2", {"start": v(67.96, 32.3) * mm, "mid": v(66.93, 31.23) * mm, "end": v(66.06, 30.01) * mm});
            skArc(sketch, "E25.30.3", {"start": v(66.06, 30.01) * mm, "mid": v(65.48, 28.25) * mm, "end": v(65.76, 26.42) * mm});
            skArc(sketch, "E25.30.4", {"start": v(68.46, 24.04) * mm, "mid": v(66.83, 24.91) * mm, "end": v(65.76, 26.42) * mm});
            skArc(sketch, "E25.30.5", {"start": v(71.42, 23.7) * mm, "mid": v(69.93, 23.77) * mm, "end": v(68.46, 24.04) * mm});
            skLineSegment(sketch, "E25.30.6", {"start": v(71.42, 23.7) * mm, "end": v(72.53, 23.74) * mm});
            skArc(sketch, "E25.30.7", {"start": v(72.53, 23.74) * mm, "mid": v(74.05, 23.6) * mm, "end": v(75.5, 23.12) * mm});
            skArc(sketch, "E25.31.0", {"start": v(62.21, 44.2) * mm, "mid": v(63.01, 45.5) * mm, "end": v(63.48, 46.95) * mm});
            skLineSegment(sketch, "E25.31.1", {"start": v(61.53, 43.32) * mm, "end": v(62.21, 44.2) * mm});
            skArc(sketch, "E25.31.2", {"start": v(61.53, 43.32) * mm, "mid": v(60.7, 42.09) * mm, "end": v(60.04, 40.75) * mm});
            skArc(sketch, "E25.31.3", {"start": v(60.04, 40.75) * mm, "mid": v(59.77, 38.92) * mm, "end": v(60.35, 37.16) * mm});
            skArc(sketch, "E25.31.4", {"start": v(63.41, 35.27) * mm, "mid": v(61.66, 35.85) * mm, "end": v(60.35, 37.16) * mm});
            skArc(sketch, "E25.31.5", {"start": v(66.39, 35.43) * mm, "mid": v(64.9, 35.24) * mm, "end": v(63.41, 35.27) * mm});
            skLineSegment(sketch, "E25.31.6", {"start": v(66.39, 35.43) * mm, "end": v(67.47, 35.66) * mm});
            skArc(sketch, "E25.31.7", {"start": v(67.47, 35.66) * mm, "mid": v(69, 35.78) * mm, "end": v(70.5, 35.54) * mm});
            skArc(sketch, "E25.32.0", {"start": v(53.85, 54.07) * mm, "mid": v(54.42, 55.5) * mm, "end": v(54.63, 57) * mm});
            skLineSegment(sketch, "E25.32.1", {"start": v(53.32, 53.1) * mm, "end": v(53.85, 54.07) * mm});
            skArc(sketch, "E25.32.2", {"start": v(53.32, 53.1) * mm, "mid": v(52.7, 51.74) * mm, "end": v(52.29, 50.3) * mm});
            skArc(sketch, "E25.32.3", {"start": v(52.29, 50.3) * mm, "mid": v(52.33, 48.46) * mm, "end": v(53.2, 46.82) * mm});
            skArc(sketch, "E25.32.4", {"start": v(56.54, 45.48) * mm, "mid": v(54.71, 45.75) * mm, "end": v(53.2, 46.82) * mm});
            skArc(sketch, "E25.32.5", {"start": v(59.44, 46.14) * mm, "mid": v(58.02, 45.7) * mm, "end": v(56.54, 45.48) * mm});
            skLineSegment(sketch, "E25.32.6", {"start": v(59.44, 46.14) * mm, "end": v(60.48, 46.55) * mm});
            skArc(sketch, "E25.32.7", {"start": v(60.48, 46.55) * mm, "mid": v(61.95, 46.93) * mm, "end": v(63.48, 46.95) * mm});
            skArc(sketch, "E25.33.0", {"start": v(43.94, 62.4) * mm, "mid": v(44.25, 63.89) * mm, "end": v(44.21, 65.41) * mm});
            skLineSegment(sketch, "E25.33.1", {"start": v(43.58, 61.35) * mm, "end": v(43.94, 62.4) * mm});
            skArc(sketch, "E25.33.2", {"start": v(43.58, 61.35) * mm, "mid": v(43.2, 59.9) * mm, "end": v(43.03, 58.42) * mm});
            skArc(sketch, "E25.33.3", {"start": v(43.03, 58.42) * mm, "mid": v(43.39, 56.6) * mm, "end": v(44.52, 55.14) * mm});
            skArc(sketch, "E25.33.4", {"start": v(48.04, 54.38) * mm, "mid": v(46.2, 54.34) * mm, "end": v(44.52, 55.14) * mm});
            skArc(sketch, "E25.33.5", {"start": v(50.79, 55.53) * mm, "mid": v(49.46, 54.85) * mm, "end": v(48.04, 54.38) * mm});
            skLineSegment(sketch, "E25.33.6", {"start": v(50.79, 55.53) * mm, "end": v(51.74, 56.1) * mm});
            skArc(sketch, "E25.33.7", {"start": v(51.74, 56.1) * mm, "mid": v(53.13, 56.72) * mm, "end": v(54.63, 57) * mm});
            skArc(sketch, "E25.34.0", {"start": v(32.76, 68.92) * mm, "mid": v(32.82, 70.45) * mm, "end": v(32.52, 71.94) * mm});
            skLineSegment(sketch, "E25.34.1", {"start": v(32.59, 67.83) * mm, "end": v(32.76, 68.92) * mm});
            skArc(sketch, "E25.34.2", {"start": v(32.59, 67.83) * mm, "mid": v(32.46, 66.34) * mm, "end": v(32.54, 64.85) * mm});
            skArc(sketch, "E25.34.3", {"start": v(32.54, 64.85) * mm, "mid": v(33.2, 63.12) * mm, "end": v(34.56, 61.87) * mm});
            skArc(sketch, "E25.34.4", {"start": v(38.16, 61.71) * mm, "mid": v(36.34, 61.37) * mm, "end": v(34.56, 61.87) * mm});
            skArc(sketch, "E25.34.5", {"start": v(40.67, 63.31) * mm, "mid": v(39.48, 62.42) * mm, "end": v(38.16, 61.71) * mm});
            skLineSegment(sketch, "E25.34.6", {"start": v(40.67, 63.31) * mm, "end": v(41.52, 64.03) * mm});
            skArc(sketch, "E25.34.7", {"start": v(41.52, 64.03) * mm, "mid": v(42.78, 64.88) * mm, "end": v(44.21, 65.41) * mm});
            skArc(sketch, "E25.35.0", {"start": v(20.64, 73.47) * mm, "mid": v(20.44, 74.98) * mm, "end": v(19.9, 76.4) * mm});
            skLineSegment(sketch, "E25.35.1", {"start": v(20.65, 72.36) * mm, "end": v(20.64, 73.47) * mm});
            skArc(sketch, "E25.35.2", {"start": v(20.65, 72.36) * mm, "mid": v(20.78, 70.87) * mm, "end": v(21.11, 69.42) * mm});
            skArc(sketch, "E25.35.3", {"start": v(21.11, 69.42) * mm, "mid": v(22.05, 67.82) * mm, "end": v(23.6, 66.82) * mm});
            skArc(sketch, "E25.35.4", {"start": v(27.18, 67.28) * mm, "mid": v(25.45, 66.62) * mm, "end": v(23.6, 66.82) * mm});
            skArc(sketch, "E25.35.5", {"start": v(29.39, 69.27) * mm, "mid": v(28.36, 68.2) * mm, "end": v(27.18, 67.28) * mm});
            skLineSegment(sketch, "E25.35.6", {"start": v(29.39, 69.27) * mm, "end": v(30.1, 70.13) * mm});
            skArc(sketch, "E25.35.7", {"start": v(30.1, 70.13) * mm, "mid": v(31.2, 71.18) * mm, "end": v(32.52, 71.94) * mm});
            skArc(sketch, "E25.36.0", {"start": v(7.93, 75.9) * mm, "mid": v(7.48, 77.36) * mm, "end": v(6.7, 78.67) * mm});
            skLineSegment(sketch, "E25.36.1", {"start": v(8.13, 74.81) * mm, "end": v(7.93, 75.9) * mm});
            skArc(sketch, "E25.36.2", {"start": v(8.13, 74.81) * mm, "mid": v(8.5, 73.37) * mm, "end": v(9.08, 71.99) * mm});
            skArc(sketch, "E25.36.3", {"start": v(9.08, 71.99) * mm, "mid": v(10.27, 70.58) * mm, "end": v(11.98, 69.85) * mm});
            skArc(sketch, "E25.36.4", {"start": v(15.42, 70.9) * mm, "mid": v(13.82, 69.97) * mm, "end": v(11.98, 69.85) * mm});
            skArc(sketch, "E25.36.5", {"start": v(17.26, 73.24) * mm, "mid": v(16.42, 72) * mm, "end": v(15.42, 70.9) * mm});
            skLineSegment(sketch, "E25.36.6", {"start": v(17.26, 73.24) * mm, "end": v(17.81, 74.2) * mm});
            skArc(sketch, "E25.36.7", {"start": v(17.81, 74.2) * mm, "mid": v(18.72, 75.43) * mm, "end": v(19.9, 76.4) * mm});
            skSolve(sketch);
        }
        {
            var Q0;
            Q0 = qSketchRegion(id + "F3", true);
            extrude(context, id + "F4", {"entities" : qUnion([Q0]), "operationType" : NewBodyOperationType.INTERSECT, "endBound" : BoundingType.THROUGH_ALL, "oppositeDirection" : true, "depth" : 25.4 * mm});
        }
    });
